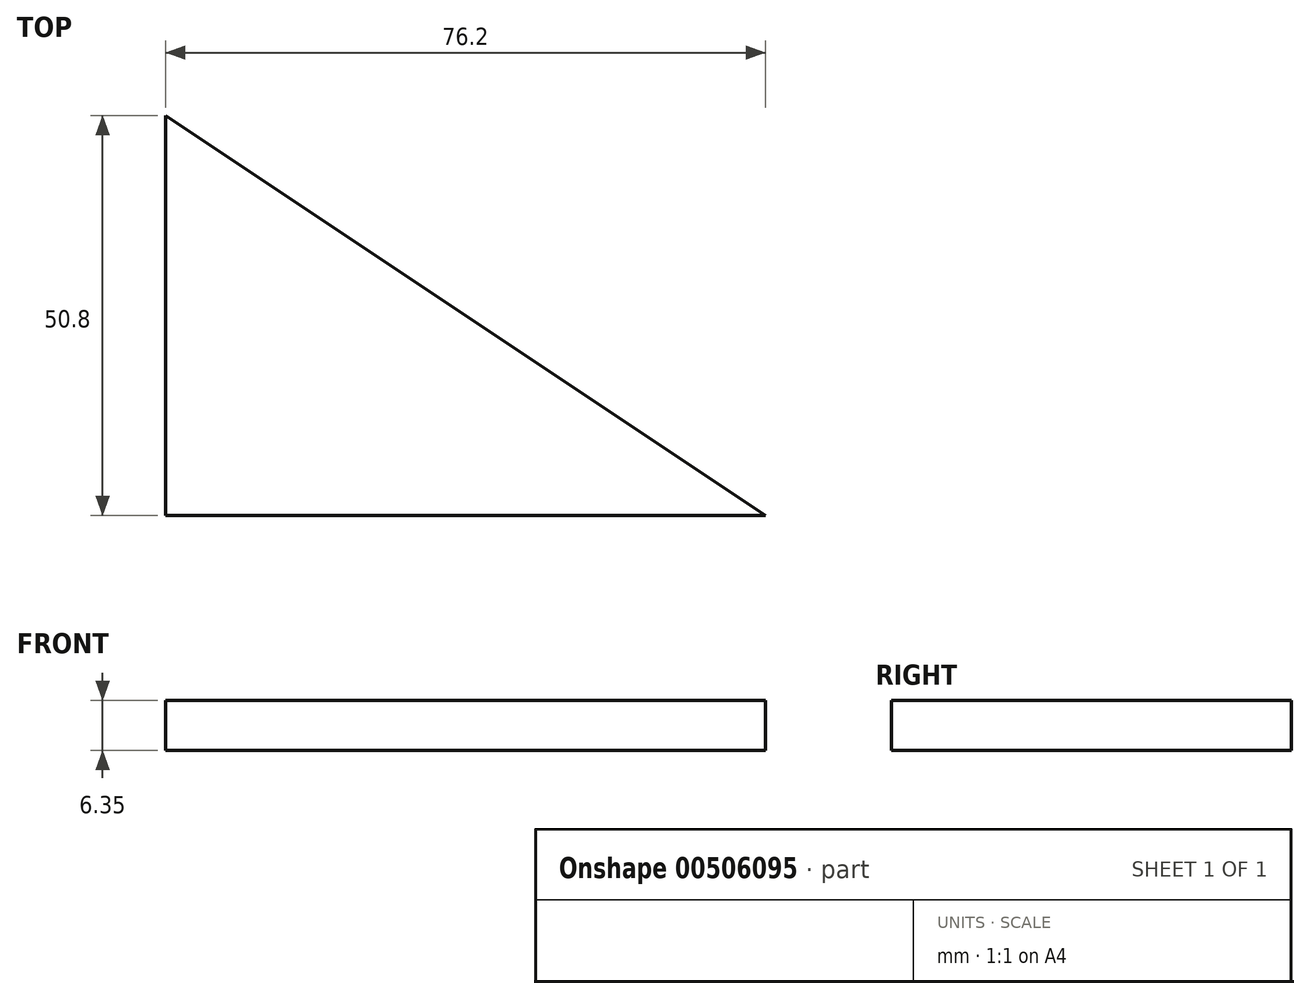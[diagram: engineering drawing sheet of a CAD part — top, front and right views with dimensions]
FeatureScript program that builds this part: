
annotation { "Feature Type Name" : "Feature", "Feature Type Description" : "" }
export const myFeature = defineFeature(function(context is Context, id is Id, definition is map)
    precondition{}
    {
        {
            var Q0;
            Q0=qCreatedBy(makeId("Top.planeOp"),FACE);
            var sketch = newSketch(context, id + "F0", { "sketchPlane" : qUnion([Q0])});
            skLineSegment(sketch, "E0.bottom", {"start": v(0, 0) * mm, "end": v(76.2, 0) * mm});
            skLineSegment(sketch, "E0.left", {"start": v(0, 0) * mm, "end": v(0, 50.8) * mm});
            skLineSegment(sketch, "E1", {"start": v(0, 50.8) * mm, "end": v(76.2, 0) * mm});
            skSolve(sketch);
        }
        {
            var Q0;
            Q0 = qSketchRegion(id + "F0", true);
            extrude(context, id + "F1", {"entities" : qUnion([Q0]), "depth" : 6.35 * mm});
        }
    });
